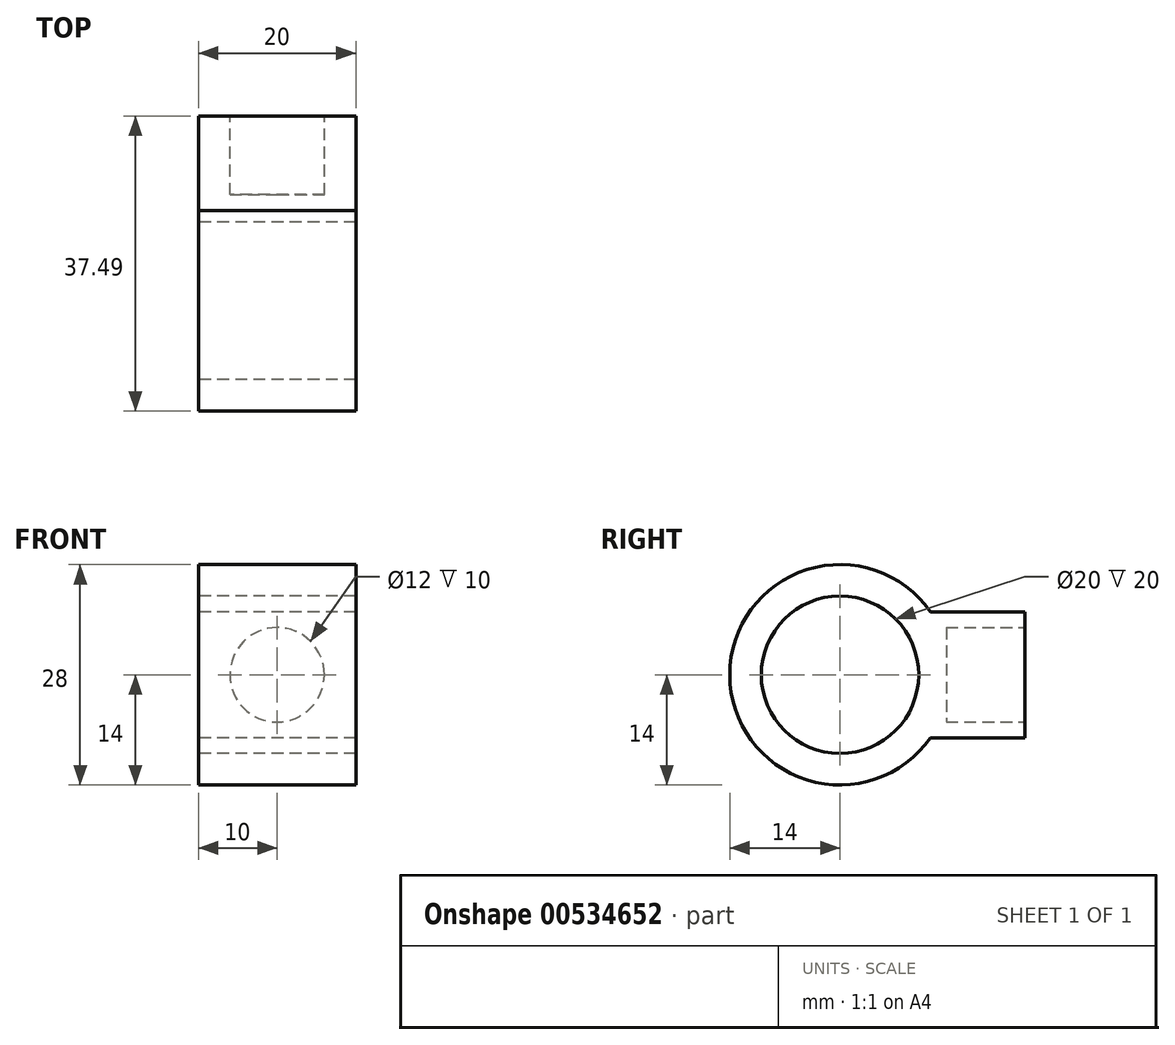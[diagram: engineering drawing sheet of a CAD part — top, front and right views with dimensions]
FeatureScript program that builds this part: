
annotation { "Feature Type Name" : "Feature", "Feature Type Description" : "" }
export const myFeature = defineFeature(function(context is Context, id is Id, definition is map)
    precondition{}
    {
        {
            var Q0;
            Q0=qCreatedBy(makeId("Right.planeOp"),FACE);
            var sketch = newSketch(context, id + "F0", { "sketchPlane" : qUnion([Q0])});
            skArc(sketch, "E0", {"start": v(11.49, 8) * mm, "mid": v(-14, 0) * mm, "end": v(11.49, -8) * mm});
            skLineSegment(sketch, "E1.bottom", {"start": v(11.49, 8) * mm, "end": v(23.49, 8) * mm});
            skLineSegment(sketch, "E1.top", {"start": v(11.49, -8) * mm, "end": v(23.49, -8) * mm});
            skLineSegment(sketch, "E1.right", {"start": v(23.49, 8) * mm, "end": v(23.49, -8) * mm});
            skCircle(sketch, "E2", {"center": v(0, 0) * mm, "radius": 10 * mm});
            skSolve(sketch);
        }
        {
            var Q0;
            Q0 = qSketchRegion(id + "F0", true);
            extrude(context, id + "F1", {"entities" : qUnion([Q0]), "depth" : 20 * mm, "offsetDistance" : 25 * mm});
        }
        {
            var Q0;
            Q0=makeQuery(id+"F1.opExtrude","SWEPT_FACE",FACE,{"disambiguationData":[OSD([sQuery(id+"F0.wireOp",EDGE,"E1.right")])]});
            var sketch = newSketch(context, id + "F2", { "sketchPlane" : qUnion([Q0])});
            skCircle(sketch, "E3", {"center": v(-10, 0) * mm, "radius": 6 * mm});
            skPoint(sketch, "E3.centerSnap0", {"position": v(-10, 8) * mm});
            skPoint(sketch, "E3.centerSnap1", {"position": v(-20, 0) * mm});
            skSolve(sketch);
        }
        {
            var Q0;
            Q0 = qSketchRegion(id + "F2", true);
            extrude(context, id + "F3", {"entities" : qUnion([Q0]), "operationType" : NewBodyOperationType.REMOVE, "oppositeDirection" : true, "depth" : 10 * mm, "offsetDistance" : 25 * mm});
        }
    });
